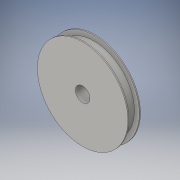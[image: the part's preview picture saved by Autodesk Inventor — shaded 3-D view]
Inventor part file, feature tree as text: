
AUTODESK INVENTOR PART (.ipt)
format: ipt  version: 2016 (Build 200138000, 138)  size: 157,184 bytes
history: native  units: in
note: dims shown in document units (in); Inventor stores cm internally (conversion verified against a paired STEP export)
features: sketch x6, extrude x5
ambient origin geometry x8: Origin, YZ Plane, XZ Plane, XY Plane, X Axis, Y Axis, Z Axis, Center Point
bodies: Solid1 (feature_tree)
feature tree (11):
  extrude  "Extrusion1"  Depth=0.196in TaperAngle=0.0deg
  extrude  "Extrusion8"  Depth=0.02in TaperAngle=0.0deg
  extrude  "Extrusion9"  Depth=0.02in
  extrude  "Extrusion10"  Depth=0.04in TaperAngle=0.0deg
  extrude  "Extrusion11"  [1 undecoded]
  sketch  "Sketch15"
  sketch  "Sketch1"  dims[d0=1.516in d1=0.196in d2=0.0in]
  sketch  "Sketch11"  dims[d30=1.7in d31=0.02in d32=0.0in]
  sketch  "Sketch12"  dims[d33=0.02in d34=0.0in d35=0.274in]
  sketch  "Sketch13"  dims[d36=0.02in d37=0.0in d38=0.04in d39=0.0in]
  sketch  "Sketch14"
note: 1 required parameter value undecoded (feature->parameter linkage not recoverable at this tier; creation-order binding heuristic only, values carry confidence <= 0.55)
